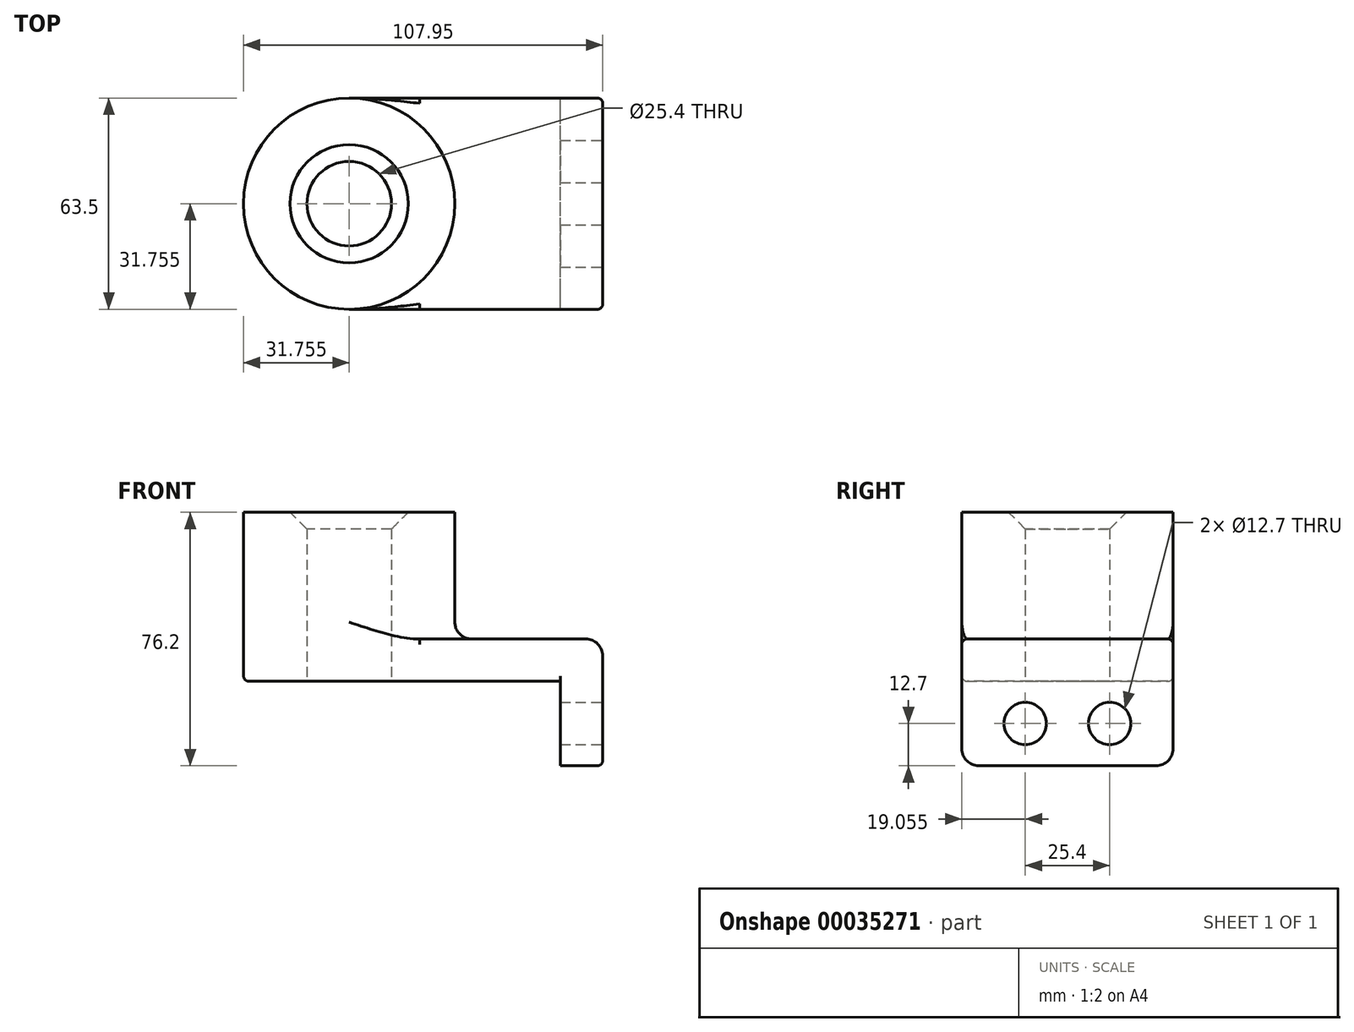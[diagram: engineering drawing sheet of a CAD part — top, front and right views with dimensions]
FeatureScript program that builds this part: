
annotation { "Feature Type Name" : "Feature", "Feature Type Description" : "" }
export const myFeature = defineFeature(function(context is Context, id is Id, definition is map)
    precondition{}
    {
        {
            var Q0;
            Q0=qCreatedBy(makeId("Top.planeOp"),FACE);
            var sketch = newSketch(context, id + "F0", { "sketchPlane" : qUnion([Q0])});
            skLineSegment(sketch, "E0.rect.bottom", {"start": v(31.3, 26.16) * mm, "end": v(-44.9, 26.16) * mm});
            skLineSegment(sketch, "E0.rect.top", {"start": v(31.3, -37.34) * mm, "end": v(-44.9, -37.34) * mm});
            skLineSegment(sketch, "E0.rect.left", {"start": v(31.3, 26.16) * mm, "end": v(31.3, -37.34) * mm});
            skLineSegment(sketch, "E0.rect.right", {"start": v(-44.9, 26.16) * mm, "end": v(-44.9, -37.34) * mm});
            skCircle(sketch, "E1", {"center": v(-44.9, -5.59) * mm, "radius": 31.75 * mm});
            skCircle(sketch, "E2", {"center": v(-44.9, -5.59) * mm, "radius": 12.7 * mm});
            skSolve(sketch);
        }
        {
            var Q0;
            Q0 = qSketchRegion(id + "F0", true);
            extrude(context, id + "F1", {"entities" : qUnion([Q0]), "depth" : 12.7 * mm});
        }
        {
            var Q0;
            {var subQ0=sQuery(id+"F0.wireOp",EDGE,"E2");var subQ1=sQuery(id+"F0.wireOp",EDGE,"E0.rect.right");var subQ3=makeQuery(id+"F0.imprint","INTERSECT",VERTEX,{"disambiguationData":[OD(0.0)],"derivedFrom":[subQ1,subQ0]});Q0=makeQuery(id+"F0.imprint","IMPRINT",FACE,{"disambiguationData":[TD([[makeQuery(id+"F0.imprint","IMPRINT",EDGE,{"disambiguationData":[TD([[subQ3,-1.0]])],"derivedFrom":subQ0}),-1.0]])]});}
            var Q1;
            {var subQ0=sQuery(id+"F0.wireOp",EDGE,"E2");var subQ1=sQuery(id+"F0.wireOp",EDGE,"E0.rect.right");var subQ3=makeQuery(id+"F0.imprint","INTERSECT",VERTEX,{"disambiguationData":[OD(0.0)],"derivedFrom":[subQ1,subQ0]});Q1=makeQuery(id+"F0.imprint","IMPRINT",FACE,{"disambiguationData":[TD([[makeQuery(id+"F0.imprint","IMPRINT",EDGE,{"disambiguationData":[TD([[subQ3,1.0]])],"derivedFrom":subQ0}),-1.0]])]});}
            extrude(context, id + "F2", {"entities" : qUnion([Q0, Q1]), "operationType" : NewBodyOperationType.ADD, "depth" : 50.8 * mm});
        }
        {
            var Q0;
            Q0=makeQuery(id+"F1.opExtrude","SWEPT_FACE",FACE,{"disambiguationData":[OSD([sQuery(id+"F0.wireOp",EDGE,"E0.rect.left")])]});
            var sketch = newSketch(context, id + "F3", { "sketchPlane" : qUnion([Q0])});
            skLineSegment(sketch, "E3.bottom", {"start": v(-37.34, 12.7) * mm, "end": v(26.16, 12.7) * mm});
            skLineSegment(sketch, "E3.top", {"start": v(-37.34, -25.4) * mm, "end": v(26.16, -25.4) * mm});
            skLineSegment(sketch, "E3.left", {"start": v(-37.34, 12.7) * mm, "end": v(-37.34, -25.4) * mm});
            skLineSegment(sketch, "E3.right", {"start": v(26.16, 12.7) * mm, "end": v(26.16, -25.4) * mm});
            skCircle(sketch, "E4", {"center": v(-18.29, -12.7) * mm, "radius": 6.35 * mm});
            skLineSegment(sketch, "E5", {"start": v(-5.59, 0) * mm, "end": v(-5.59, -25.4) * mm, "construction": true});
            skCircle(sketch, "E6.MirrorC", {"center": v(7.11, -12.7) * mm, "radius": 6.35 * mm});
            skSolve(sketch);
        }
        {
            var Q0;
            {var subQ2=sQuery(id+"F3.wireOp",EDGE,"E3.bottom");Q0=makeQuery(id+"F3.imprint","IMPRINT",FACE,{"disambiguationData":[TD([[makeQuery(id+"F3.imprint","IMPRINT",EDGE,{"derivedFrom":subQ2}),1.0]])]});}
            var Q1;
            {var subQ2=sQuery(id+"F3.wireOp",EDGE,"E3.top");Q1=makeQuery(id+"F3.imprint","IMPRINT",FACE,{"disambiguationData":[TD([[makeQuery(id+"F3.imprint","IMPRINT",EDGE,{"derivedFrom":subQ2}),1.0]])]});}
            extrude(context, id + "F4", {"entities" : qUnion([Q0, Q1]), "operationType" : NewBodyOperationType.ADD, "oppositeDirection" : true, "depth" : 12.7 * mm});
        }
        {
            var Q0;
            {var subQ0=sQuery(id+"F0.wireOp",EDGE,"E1");Q0=makeQuery(id+"F2.boolean.opBoolean","INTERSECT",EDGE,{"derivedFrom":[makeQuery(id+"F1.opExtrude","CAP_FACE",FACE,{"disambiguationData":[OSD([sQuery(id+"F0.wireOp",EDGE,"E0.rect.bottom"),sQuery(id+"F0.wireOp",EDGE,"E0.rect.top"),sQuery(id+"F0.wireOp",EDGE,"E0.rect.left"),subQ0,sQuery(id+"F0.wireOp",EDGE,"E2")])],"isStart":false}),makeQuery(id+"F2.opExtrude","SWEPT_FACE",FACE,{"disambiguationData":[OSD([subQ0])]})]});}
            var Q1;
            Q1=makeQuery(id+"F4.opExtrude","SWEPT_EDGE",EDGE,{"disambiguationData":[OSD([sQuery(id+"F3.wireOp",EDGE,"E3.top"),sQuery(id+"F3.wireOp",EDGE,"E3.left")])]});
            var Q2;
            Q2=makeQuery(id+"F4.opExtrude","SWEPT_EDGE",EDGE,{"disambiguationData":[OSD([sQuery(id+"F3.wireOp",EDGE,"E3.top"),sQuery(id+"F3.wireOp",EDGE,"E3.right")])]});
            var Q3;
            Q3=makeQuery(id+"F1.opExtrude","CAP_EDGE",EDGE,{"disambiguationData":[OSD([sQuery(id+"F0.wireOp",EDGE,"E0.rect.left")])],"isStart":false});
            fillet(context, id + "F5", {"entities" : qUnion([Q0, Q1, Q2, Q3]), "radius" : 5.08 * mm, "tangentPropagation" : true, "allowEdgeOverflow" : false});
        }
        {
            var Q0;
            Q0=makeQuery(id+"F1.opExtrude","CAP_EDGE",EDGE,{"disambiguationData":[OSD([sQuery(id+"F0.wireOp",EDGE,"E0.rect.top")])],"isStart":false});
            var Q1;
            Q1=makeQuery(id+"F1.opExtrude","CAP_EDGE",EDGE,{"disambiguationData":[OSD([sQuery(id+"F0.wireOp",EDGE,"E0.rect.top")])],"isStart":true});
            fillet(context, id + "F6", {"entities" : qUnion([Q0, Q1]), "radius" : 1.59 * mm, "tangentPropagation" : true, "allowEdgeOverflow" : false});
        }
        {
            var Q0;
            Q0=makeQuery(id+"F2.opExtrude","CAP_EDGE",EDGE,{"disambiguationData":[OSD([sQuery(id+"F0.wireOp",EDGE,"E2")])],"isStart":false});
            chamfer(context, id + "F7", {"entities" : qUnion([Q0]), "width" : 5.08 * mm, "tangentPropagation" : true});
        }
    });
